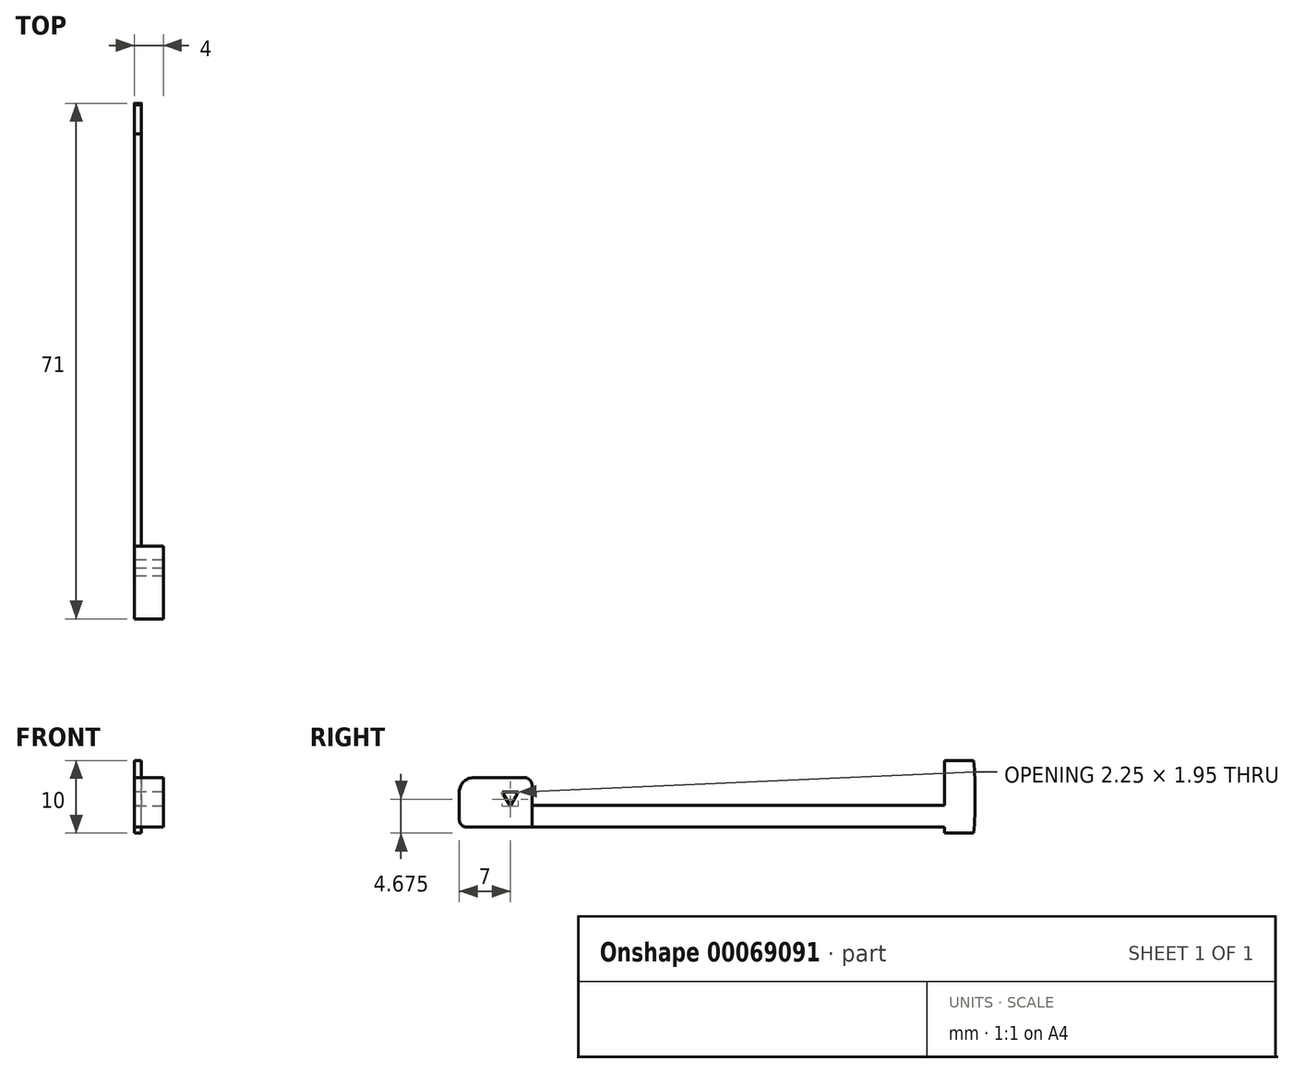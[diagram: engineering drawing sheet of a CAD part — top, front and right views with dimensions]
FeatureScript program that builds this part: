
annotation { "Feature Type Name" : "Feature", "Feature Type Description" : "" }
export const myFeature = defineFeature(function(context is Context, id is Id, definition is map)
    precondition{}
    {
        {
            var Q0;
            Q0=qCreatedBy(makeId("Right.planeOp"),FACE);
            var sketch = newSketch(context, id + "F0", { "sketchPlane" : qUnion([Q0])});
            skCircle(sketch, "E0.cCircle", {"center": v(0, 0) * mm, "radius": 0.65 * mm, "construction": true});
            skLineSegment(sketch, "E0.0", {"start": v(-1.13, 0.65) * mm, "end": v(1.13, 0.65) * mm});
            skLineSegment(sketch, "E0.1", {"start": v(1.13, 0.65) * mm, "end": v(0, -1.3) * mm});
            skLineSegment(sketch, "E0.2", {"start": v(0, -1.3) * mm, "end": v(-1.13, 0.65) * mm});
            skPoint(sketch, "E0.0.midPoint", {"position": v(0, 0.65) * mm});
            skLineSegment(sketch, "E1", {"start": v(-2, -1.15) * mm, "end": v(-16, -1.15) * mm, "construction": true});
            skLineSegment(sketch, "E2", {"start": v(-16, 0) * mm, "end": v(-16, -2.3) * mm, "construction": true});
            skLineSegment(sketch, "E3.bottom", {"start": v(-6, -4.15) * mm, "end": v(3, -4.15) * mm});
            skLineSegment(sketch, "E3.top", {"start": v(-5, 2.65) * mm, "end": v(2, 2.65) * mm});
            skLineSegment(sketch, "E3.left", {"start": v(-7, -3.15) * mm, "end": v(-7, 0.65) * mm});
            skLineSegment(sketch, "E3.right", {"start": v(3, -4.15) * mm, "end": v(3, 1.65) * mm});
            skCircle(sketch, "E4", {"center": v(-16, 15) * mm, "radius": 15 * mm, "construction": true});
            skPoint(sketch, "E5.visualSharp", {"position": v(-7, 2.65) * mm});
            skArc(sketch, "E5.filletArc", {"start": v(-5, 2.65) * mm, "mid": v(-6.41, 2.06) * mm, "end": v(-7, 0.65) * mm});
            skPoint(sketch, "E6.visualSharp", {"position": v(-7, -4.15) * mm});
            skArc(sketch, "E6.filletArc", {"start": v(-7, -3.15) * mm, "mid": v(-6.7, -3.86) * mm, "end": v(-6, -4.15) * mm});
            skPoint(sketch, "E7.visualSharp", {"position": v(3, 2.65) * mm});
            skArc(sketch, "E7.filletArc", {"start": v(3, 1.65) * mm, "mid": v(2.7, 2.36) * mm, "end": v(2, 2.65) * mm});
            skLineSegment(sketch, "E8", {"start": v(3, -4.15) * mm, "end": v(59.8, -4.15) * mm});
            skLineSegment(sketch, "E9", {"start": v(3, -1.15) * mm, "end": v(59.8, -1.15) * mm});
            skArc(sketch, "E10", {"start": v(63.8, -5) * mm, "mid": v(64, 0) * mm, "end": v(63.8, 5) * mm});
            skLineSegment(sketch, "E11", {"start": v(63.8, 5) * mm, "end": v(59.8, 5) * mm});
            skLineSegment(sketch, "E12", {"start": v(59.8, 5) * mm, "end": v(59.8, -1.15) * mm});
            skLineSegment(sketch, "E13", {"start": v(59.8, -4.15) * mm, "end": v(59.8, -5) * mm});
            skLineSegment(sketch, "E14", {"start": v(59.8, -5) * mm, "end": v(63.8, -5) * mm});
            skSolve(sketch);
        }
        {
            var Q0;
            Q0=makeQuery(id+"F0.imprint","IMPRINT",FACE,{"disambiguationData":[TD([[makeQuery(id+"F0.imprint","IMPRINT",EDGE,{"derivedFrom":sQuery(id+"F0.wireOp",EDGE,"E0.0")}),1.0]])]});
            extrude(context, id + "F1", {"entities" : qUnion([Q0]), "depth" : 3 * mm, "hasSecondDirection" : true, "secondDirectionOppositeDirection" : true, "secondDirectionDepth" : 1 * mm});
        }
        {
            var Q0;
            {var subQ0=sQuery(id+"F0.wireOp",EDGE,"E8");Q0=makeQuery(id+"F0.imprint","IMPRINT",FACE,{"disambiguationData":[TD([[makeQuery(id+"F0.imprint","IMPRINT",EDGE,{"derivedFrom":subQ0}),1.0]])]});}
            var Q1;
            Q1=makeQuery(id+"F1.opExtrude","CAP_FACE",FACE,{"disambiguationData":[OSD([sQuery(id+"F0.wireOp",EDGE,"E0.0"),sQuery(id+"F0.wireOp",EDGE,"E0.1"),sQuery(id+"F0.wireOp",EDGE,"E0.2"),sQuery(id+"F0.wireOp",EDGE,"E3.bottom"),sQuery(id+"F0.wireOp",EDGE,"E3.top"),sQuery(id+"F0.wireOp",EDGE,"E3.left"),sQuery(id+"F0.wireOp",EDGE,"E3.right"),sQuery(id+"F0.wireOp",EDGE,"E5.filletArc"),sQuery(id+"F0.wireOp",EDGE,"E6.filletArc"),sQuery(id+"F0.wireOp",EDGE,"E7.filletArc")])],"isStart":true});
            extrude(context, id + "F2", {"entities" : qUnion([Q0]), "operationType" : NewBodyOperationType.ADD, "endBound" : BoundingType.UP_TO_SURFACE, "oppositeDirection" : true, "endBoundEntityFace" : qUnion([Q1]), "depth" : 25 * mm});
        }
    });
